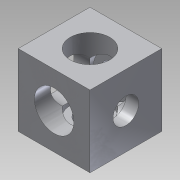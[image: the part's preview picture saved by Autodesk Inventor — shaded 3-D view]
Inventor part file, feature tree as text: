
AUTODESK INVENTOR PART (.ipt)
format: ipt  version: 2013 SP2 (Build 170200200, 200)  size: 132,608 bytes
history: native  units: mm
features: sketch x4, extrude x3, other x2, pattern_circular x2
ambient origin geometry x8: Origin, YZ Plane, XZ Plane, XY Plane, X Axis, Y Axis, Z Axis, Center Point
bodies: Solid1 (feature_tree)
feature tree (11):
  extrude  "Extrusion1"  Depth=20.0mm
  sketch  "Sketch2"  dims[d2=20.0mm d3=0.0mm d4=7.14mm]
  extrude  "Extrusion2"  Depth=7.14mm
  extrude  "Extrusion3"  Depth=20.0mm TaperAngle=0.0deg
  sketch  "Sketch3"  dims[d5=11.0mm d6=20.0mm d7=0.0mm]
  other  "Work Axis1"
  sketch  "Sketch4"  dims[d8=16.5mm d9=0.0mm d10=20.0mm d11=90.0deg d13=20.0mm d14=90.0deg]
  other  "Work Axis2"
  pattern_circular  "Circular Pattern1"  Count=2 Angle=90.0deg
  pattern_circular  "Circular Pattern2"  Count=2 Angle=90.0deg
  sketch  "Sketch1"  dims[d0=20.0mm d1=20.0mm]
